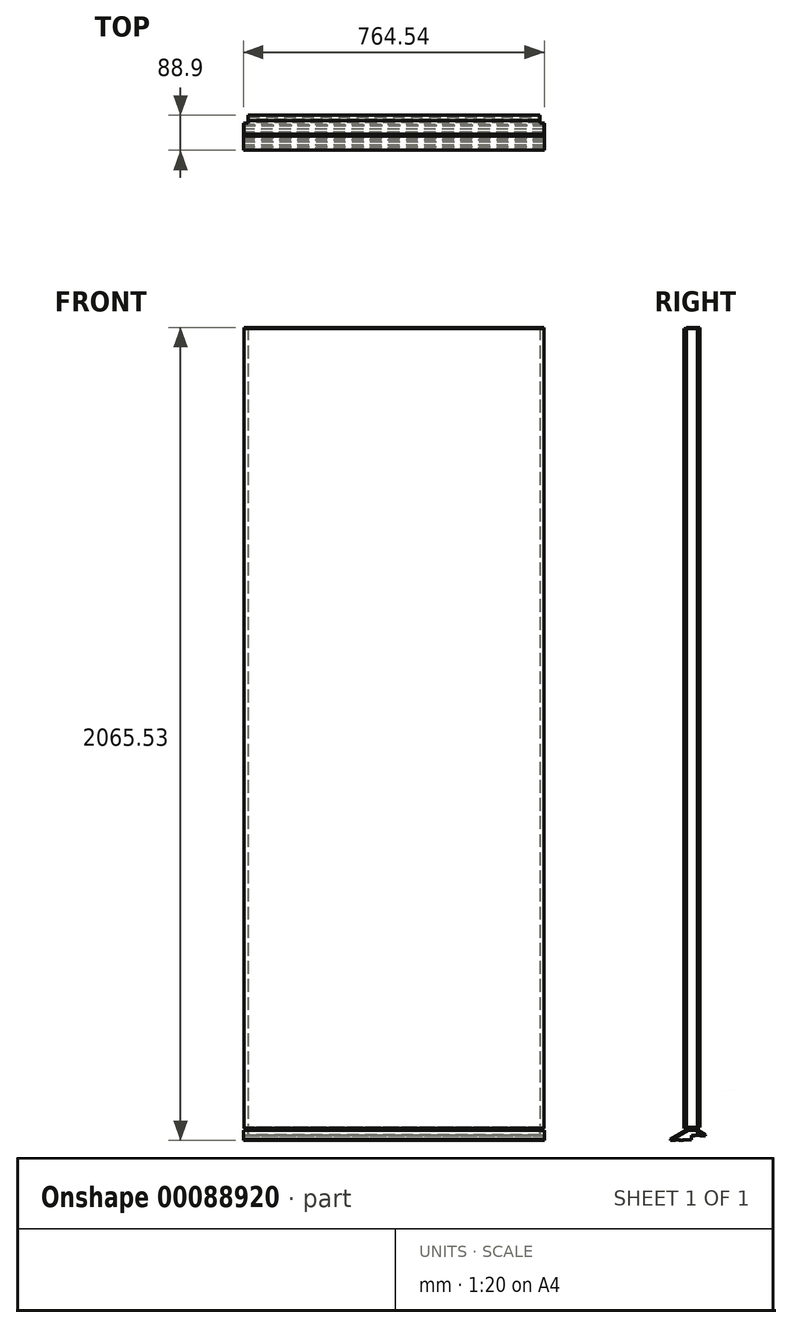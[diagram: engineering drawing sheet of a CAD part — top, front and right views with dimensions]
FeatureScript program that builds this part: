
annotation { "Feature Type Name" : "Feature", "Feature Type Description" : "" }
export const myFeature = defineFeature(function(context is Context, id is Id, definition is map)
    precondition{}
    {
        {
            var Q0;
            Q0=qCreatedBy(makeId("Right.planeOp"),FACE);
            var sketch = newSketch(context, id + "F0", { "sketchPlane" : qUnion([Q0])});
            skLineSegment(sketch, "E0.bottom", {"start": v(-1219.2, -50.8) * mm, "end": v(1219.2, -50.8) * mm});
            skLineSegment(sketch, "E0.top", {"start": v(-1219.2, 0) * mm, "end": v(1219.2, 0) * mm});
            skLineSegment(sketch, "E0.left", {"start": v(-1219.2, -50.8) * mm, "end": v(-1219.2, 0) * mm});
            skLineSegment(sketch, "E0.right", {"start": v(1219.2, -50.8) * mm, "end": v(1219.2, 0) * mm});
            skPoint(sketch, "E1", {"position": v(0, 0) * mm});
            skLineSegment(sketch, "E2", {"start": v(0, 0) * mm, "end": v(0, 11.43) * mm});
            skLineSegment(sketch, "E3", {"start": v(0, 11.43) * mm, "end": v(1219.2, 11.43) * mm});
            skLineSegment(sketch, "E4", {"start": v(1219.2, 11.43) * mm, "end": v(1219.2, 0) * mm});
            skLineSegment(sketch, "E5", {"start": v(0, 9.65) * mm, "end": v(1219.2, 9.65) * mm});
            skLineSegment(sketch, "E6.bottom", {"start": v(-18.03, 30.73) * mm, "end": v(16.5, 30.73) * mm});
            skLineSegment(sketch, "E6.top", {"start": v(-18.03, 2062.73) * mm, "end": v(16.5, 2062.73) * mm});
            skLineSegment(sketch, "E6.left", {"start": v(-18.03, 30.73) * mm, "end": v(-18.03, 2062.73) * mm});
            skLineSegment(sketch, "E6.right", {"start": v(16.5, 30.73) * mm, "end": v(16.5, 2062.73) * mm});
            skLineSegment(sketch, "E7", {"start": v(-18.03, 35.05) * mm, "end": v(16.5, 35.05) * mm});
            skLineSegment(sketch, "E8", {"start": v(6.35, 0) * mm, "end": v(6.35, 11.43) * mm});
            skSolve(sketch);
        }
        {
            var Q0;
            Q0=qCreatedBy(makeId("Right.planeOp"),FACE);
            var sketch = newSketch(context, id + "F1", { "sketchPlane" : qUnion([Q0])});
            skLineSegment(sketch, "E9.bottom", {"start": v(-1219.2, -50.8) * mm, "end": v(1219.2, -50.8) * mm});
            skLineSegment(sketch, "E9.top", {"start": v(-1219.2, 0) * mm, "end": v(1219.2, 0) * mm});
            skLineSegment(sketch, "E9.left", {"start": v(-1219.2, -50.8) * mm, "end": v(-1219.2, 0) * mm});
            skLineSegment(sketch, "E9.right", {"start": v(1219.2, -50.8) * mm, "end": v(1219.2, 0) * mm});
            skPoint(sketch, "E10", {"position": v(0, 0) * mm});
            skLineSegment(sketch, "E11", {"start": v(0, 0) * mm, "end": v(0, 11.94) * mm});
            skLineSegment(sketch, "E12", {"start": v(0, 11.94) * mm, "end": v(1219.2, 11.94) * mm});
            skLineSegment(sketch, "E13", {"start": v(1219.2, 11.94) * mm, "end": v(1219.2, 0) * mm});
            skLineSegment(sketch, "E14", {"start": v(0, 9.4) * mm, "end": v(1219.2, 9.4) * mm});
            skLineSegment(sketch, "E15.bottom", {"start": v(-12.45, 33.53) * mm, "end": v(22.1, 33.53) * mm});
            skLineSegment(sketch, "E15.top", {"start": v(-12.45, 2065.53) * mm, "end": v(22.1, 2065.53) * mm});
            skLineSegment(sketch, "E15.left", {"start": v(-12.45, 33.53) * mm, "end": v(-12.45, 2065.53) * mm});
            skLineSegment(sketch, "E15.right", {"start": v(22.1, 33.53) * mm, "end": v(22.1, 2065.53) * mm});
            skLineSegment(sketch, "E16", {"start": v(-12.45, 37.85) * mm, "end": v(22.1, 37.85) * mm});
            skLineSegment(sketch, "E17", {"start": v(9.4, 0) * mm, "end": v(9.4, 11.94) * mm});
            skSolve(sketch);
        }
        {
            var Q0;
            {var subQ0=sQuery(id+"F0.wireOp",EDGE,"E6.bottom");Q0=makeQuery(id+"F0.imprint","IMPRINT",FACE,{"disambiguationData":[TD([[makeQuery(id+"F0.imprint","IMPRINT",EDGE,{"derivedFrom":subQ0}),1.0]])]});}
            var Q1;
            {var subQ0=sQuery(id+"F0.wireOp",EDGE,"E6.top");Q1=makeQuery(id+"F0.imprint","IMPRINT",FACE,{"disambiguationData":[TD([[makeQuery(id+"F0.imprint","IMPRINT",EDGE,{"derivedFrom":subQ0}),-1.0]])]});}
            extrude(context, id + "F2", {"entities" : qUnion([Q0, Q1]), "endBound" : BoundingType.SYMMETRIC, "depth" : 762 * mm});
        }
        {
            var Q0;
            {var subQ0=sQuery(id+"F1.wireOp",EDGE,"E15.top");Q0=makeQuery(id+"F1.imprint","IMPRINT",FACE,{"disambiguationData":[TD([[makeQuery(id+"F1.imprint","IMPRINT",EDGE,{"derivedFrom":subQ0}),-1.0]])]});}
            var Q1;
            {var subQ0=sQuery(id+"F1.wireOp",EDGE,"E15.bottom");Q1=makeQuery(id+"F1.imprint","IMPRINT",FACE,{"disambiguationData":[TD([[makeQuery(id+"F1.imprint","IMPRINT",EDGE,{"derivedFrom":subQ0}),1.0]])]});}
            extrude(context, id + "F3", {"entities" : qUnion([Q0, Q1]), "endBound" : BoundingType.SYMMETRIC, "depth" : 762 * mm});
        }
        {
            var Q0;
            Q0=qCreatedBy(makeId("Right.planeOp"),FACE);
            var sketch = newSketch(context, id + "F4", { "sketchPlane" : qUnion([Q0])});
            skLineSegment(sketch, "E18", {"start": v(0, 11.83) * mm, "end": v(0, 0) * mm});
            skLineSegment(sketch, "E19", {"start": v(0, 0) * mm, "end": v(-9.31, 0) * mm});
            skLineSegment(sketch, "E20", {"start": v(-53.34, 0) * mm, "end": v(-53.34, 2.54) * mm});
            skLineSegment(sketch, "E21", {"start": v(-53.34, 2.54) * mm, "end": v(-13.75, 25.4) * mm});
            skLineSegment(sketch, "E22", {"start": v(-13.75, 25.4) * mm, "end": v(10.68, 25.4) * mm});
            skLineSegment(sketch, "E23", {"start": v(30.48, 11.43) * mm, "end": v(21.59, 11.43) * mm});
            skLineSegment(sketch, "E24", {"start": v(30.48, 11.43) * mm, "end": v(30.48, 13.97) * mm});
            skLineSegment(sketch, "E25", {"start": v(30.48, 13.97) * mm, "end": v(10.68, 25.4) * mm});
            skLineSegment(sketch, "E26", {"start": v(-44.03, 0) * mm, "end": v(-44.03, 0.8) * mm});
            skLineSegment(sketch, "E27", {"start": v(-44.03, 0.8) * mm, "end": v(-31.33, 0.8) * mm});
            skLineSegment(sketch, "E28", {"start": v(-22.01, 1.59) * mm, "end": v(-9.31, 1.59) * mm});
            skLineSegment(sketch, "E29", {"start": v(-9.31, 1.59) * mm, "end": v(-9.31, 0) * mm, "construction": true});
            skLineSegment(sketch, "E30.trimOffspring", {"start": v(-44.03, 0) * mm, "end": v(-53.34, 0) * mm});
            skLineSegment(sketch, "E31", {"start": v(8.89, 11.43) * mm, "end": v(8.89, 12.22) * mm, "construction": true});
            skLineSegment(sketch, "E32", {"start": v(8.89, 12.22) * mm, "end": v(21.59, 12.22) * mm});
            skLineSegment(sketch, "E33", {"start": v(21.59, 12.22) * mm, "end": v(21.59, 11.43) * mm});
            skLineSegment(sketch, "E34", {"start": v(8.89, 11.43) * mm, "end": v(8.89, 10.64) * mm, "construction": true});
            skLineSegment(sketch, "E35", {"start": v(8.89, 10.64) * mm, "end": v(21.59, 10.64) * mm, "construction": true});
            skLineSegment(sketch, "E36", {"start": v(21.59, 10.64) * mm, "end": v(21.59, 11.43) * mm, "construction": true});
            skLineSegment(sketch, "E37", {"start": v(-44.03, 0) * mm, "end": v(-44.03, -0.8) * mm, "construction": true});
            skLineSegment(sketch, "E38", {"start": v(-44.03, -0.8) * mm, "end": v(-31.33, -0.8) * mm, "construction": true});
            skLineSegment(sketch, "E39", {"start": v(-31.33, -0.8) * mm, "end": v(-31.33, 0) * mm, "construction": true});
            skLineSegment(sketch, "E40", {"start": v(-22.01, 0) * mm, "end": v(-22.01, -1.59) * mm, "construction": true});
            skLineSegment(sketch, "E41", {"start": v(-22.01, -1.59) * mm, "end": v(-9.31, -1.59) * mm, "construction": true});
            skLineSegment(sketch, "E42", {"start": v(-9.31, -1.59) * mm, "end": v(-9.31, 0) * mm, "construction": true});
            skLineSegment(sketch, "E43", {"start": v(-31.33, 0.8) * mm, "end": v(-31.33, 0) * mm, "construction": true});
            skLineSegment(sketch, "E44", {"start": v(-22.01, 1.59) * mm, "end": v(-22.01, 0) * mm, "construction": true});
            skLineSegment(sketch, "E45", {"start": v(-31.33, 0.8) * mm, "end": v(-31.33, 0.4) * mm});
            skLineSegment(sketch, "E46", {"start": v(-31.33, 0.4) * mm, "end": v(-22.01, 0.4) * mm});
            skLineSegment(sketch, "E47", {"start": v(-22.01, 0.4) * mm, "end": v(-22.01, 1.59) * mm});
            skLineSegment(sketch, "E48", {"start": v(-9.31, 0.8) * mm, "end": v(0, 0.8) * mm});
            skLineSegment(sketch, "E49", {"start": v(-9.31, 1.59) * mm, "end": v(-9.31, 0.8) * mm});
            skLineSegment(sketch, "E50", {"start": v(8.89, 11.83) * mm, "end": v(0, 11.83) * mm});
            skLineSegment(sketch, "E51", {"start": v(8.89, 12.22) * mm, "end": v(8.89, 11.83) * mm});
            skSolve(sketch);
        }
        {
            var Q0;
            Q0=qCreatedBy(makeId("Right.planeOp"),FACE);
            var sketch = newSketch(context, id + "F5", { "sketchPlane" : qUnion([Q0])});
            skLineSegment(sketch, "E52", {"start": v(-48.26, 0) * mm, "end": v(-48.26, 2.54) * mm});
            skLineSegment(sketch, "E53", {"start": v(-48.26, 2.54) * mm, "end": v(-8.67, 25.4) * mm});
            skLineSegment(sketch, "E54", {"start": v(-8.67, 25.4) * mm, "end": v(16.64, 25.4) * mm});
            skLineSegment(sketch, "E55", {"start": v(24.13, 11.94) * mm, "end": v(35.56, 11.94) * mm});
            skLineSegment(sketch, "E56", {"start": v(35.56, 11.94) * mm, "end": v(35.56, 14.48) * mm});
            skLineSegment(sketch, "E57", {"start": v(16.64, 25.4) * mm, "end": v(35.56, 14.48) * mm});
            skLineSegment(sketch, "E58", {"start": v(-40.64, 0) * mm, "end": v(-40.64, 0.8) * mm});
            skLineSegment(sketch, "E59", {"start": v(-40.64, 0.8) * mm, "end": v(-27.94, 0.8) * mm});
            skLineSegment(sketch, "E60", {"start": v(-20.32, 0) * mm, "end": v(-20.32, 1.59) * mm});
            skLineSegment(sketch, "E61", {"start": v(-20.32, 1.59) * mm, "end": v(-7.62, 1.59) * mm});
            skLineSegment(sketch, "E62.trimOffspring", {"start": v(-40.64, 0) * mm, "end": v(-48.26, 0) * mm});
            skLineSegment(sketch, "E63", {"start": v(11.43, 12.2) * mm, "end": v(11.43, 12.47) * mm});
            skLineSegment(sketch, "E64", {"start": v(11.43, 12.47) * mm, "end": v(24.13, 12.47) * mm});
            skLineSegment(sketch, "E65", {"start": v(24.13, 12.47) * mm, "end": v(24.13, 11.94) * mm});
            skLineSegment(sketch, "E66.trimOffspring", {"start": v(0, 12.2) * mm, "end": v(11.43, 12.2) * mm});
            skLineSegment(sketch, "E67", {"start": v(-40.64, 0.8) * mm, "end": v(-48.26, 0.8) * mm, "construction": true});
            skLineSegment(sketch, "E68", {"start": v(-7.62, 1.59) * mm, "end": v(0, 1.59) * mm, "construction": true});
            skLineSegment(sketch, "E69", {"start": v(11.43, 12.2) * mm, "end": v(11.43, 11.4) * mm, "construction": true});
            skLineSegment(sketch, "E70", {"start": v(11.43, 11.4) * mm, "end": v(24.13, 11.4) * mm, "construction": true});
            skLineSegment(sketch, "E71", {"start": v(24.13, 11.4) * mm, "end": v(24.13, 11.94) * mm, "construction": true});
            skLineSegment(sketch, "E72", {"start": v(-40.64, 0) * mm, "end": v(-40.64, -0.8) * mm, "construction": true});
            skLineSegment(sketch, "E73", {"start": v(-40.64, -0.8) * mm, "end": v(-27.94, -0.8) * mm, "construction": true});
            skLineSegment(sketch, "E74", {"start": v(-27.94, -0.8) * mm, "end": v(-27.94, 0) * mm, "construction": true});
            skLineSegment(sketch, "E75", {"start": v(-20.32, 0) * mm, "end": v(-20.32, -1.59) * mm, "construction": true});
            skLineSegment(sketch, "E76", {"start": v(-20.32, -1.59) * mm, "end": v(-7.62, -1.59) * mm, "construction": true});
            skLineSegment(sketch, "E77", {"start": v(-7.62, -1.59) * mm, "end": v(-7.62, 0) * mm, "construction": true});
            skLineSegment(sketch, "E78", {"start": v(0, 12.47) * mm, "end": v(11.43, 12.47) * mm, "construction": true});
            skLineSegment(sketch, "E79", {"start": v(24.13, 12.47) * mm, "end": v(35.56, 12.47) * mm, "construction": true});
            skLineSegment(sketch, "E80", {"start": v(-27.94, 0.8) * mm, "end": v(-20.32, 0.8) * mm, "construction": true});
            skLineSegment(sketch, "E81", {"start": v(0, 0.8) * mm, "end": v(0, 12.2) * mm});
            skLineSegment(sketch, "E82", {"start": v(-7.62, 1.59) * mm, "end": v(-7.62, 0.8) * mm});
            skLineSegment(sketch, "E83", {"start": v(-7.62, 0.8) * mm, "end": v(0, 0.8) * mm});
            skLineSegment(sketch, "E84", {"start": v(-27.94, 0.8) * mm, "end": v(-27.94, 0.4) * mm});
            skLineSegment(sketch, "E85", {"start": v(-27.94, 0.4) * mm, "end": v(-20.32, 0.4) * mm});
            skPoint(sketch, "E86", {"position": v(-40.64, 0.4) * mm});
            skPoint(sketch, "E87", {"position": v(24.13, 12.2) * mm});
            skSolve(sketch);
        }
        {
            var Q0;
            Q0=makeQuery(id+"F4.imprint","IMPRINT",FACE,{"disambiguationData":[TD([[makeQuery(id+"F4.imprint","IMPRINT",EDGE,{"derivedFrom":sQuery(id+"F4.wireOp",EDGE,"E18")}),-1.0]])]});
            extrude(context, id + "F6", {"entities" : qUnion([Q0]), "endBound" : BoundingType.SYMMETRIC, "oppositeDirection" : true, "depth" : 764.54 * mm});
        }
        {
            var Q0;
            Q0=makeQuery(id+"F5.imprint","IMPRINT",FACE,{"disambiguationData":[TD([[makeQuery(id+"F5.imprint","IMPRINT",EDGE,{"derivedFrom":sQuery(id+"F5.wireOp",EDGE,"E52")}),-1.0]])]});
            extrude(context, id + "F7", {"entities" : qUnion([Q0]), "endBound" : BoundingType.SYMMETRIC, "depth" : 764.54 * mm});
        }
        {
            var Q0;
            Q0=qCreatedBy(makeId("Top.planeOp"),FACE);
            var sketch = newSketch(context, id + "F8", { "sketchPlane" : qUnion([Q0])});
            skLineSegment(sketch, "E88.0", {"start": v(381, 16.5) * mm, "end": v(-381, 16.5) * mm, "construction": true});
            skLineSegment(sketch, "E88.1", {"start": v(-381, -18.03) * mm, "end": v(-381, 16.5) * mm, "construction": true});
            skLineSegment(sketch, "E88.2", {"start": v(381, -18.03) * mm, "end": v(-381, -18.03) * mm, "construction": true});
            skLineSegment(sketch, "E88.3", {"start": v(381, -18.03) * mm, "end": v(381, 16.5) * mm, "construction": true});
            skLineSegment(sketch, "E89", {"start": v(0, 16.5) * mm, "end": v(0, -18.03) * mm, "construction": true});
            skLineSegment(sketch, "E90.bottom", {"start": v(-381, 16.5) * mm, "end": v(-372.11, 16.5) * mm, "construction": true});
            skLineSegment(sketch, "E90.top", {"start": v(-381, 67.3) * mm, "end": v(-372.11, 67.3) * mm, "construction": true});
            skLineSegment(sketch, "E90.left", {"start": v(-381, 16.5) * mm, "end": v(-381, 67.3) * mm, "construction": true});
            skLineSegment(sketch, "E90.right", {"start": v(-372.11, 16.5) * mm, "end": v(-372.11, 67.3) * mm, "construction": true});
            skLineSegment(sketch, "E91.0", {"start": v(-382.27, 15.24) * mm, "end": v(-382.27, 68.58) * mm});
            skLineSegment(sketch, "E91.1", {"start": v(-382.27, 15.24) * mm, "end": v(-370.84, 15.24) * mm});
            skLineSegment(sketch, "E91.2", {"start": v(-370.84, 15.24) * mm, "end": v(-370.84, 68.58) * mm});
            skLineSegment(sketch, "E91.3", {"start": v(-382.27, 68.58) * mm, "end": v(-370.84, 68.58) * mm});
            skLineSegment(sketch, "E92.MirrorCS", {"start": v(382.27, 15.24) * mm, "end": v(382.27, 68.58) * mm});
            skLineSegment(sketch, "E93.MirrorCS", {"start": v(382.27, 15.24) * mm, "end": v(370.84, 15.24) * mm});
            skLineSegment(sketch, "E94.MirrorCS", {"start": v(370.84, 15.24) * mm, "end": v(370.84, 68.58) * mm});
            skLineSegment(sketch, "E95.MirrorCS", {"start": v(382.27, 68.58) * mm, "end": v(370.84, 68.58) * mm});
            skSolve(sketch);
        }
        {
            var Q0;
            Q0=qCreatedBy(makeId("Top.planeOp"),FACE);
            var sketch = newSketch(context, id + "F9", { "sketchPlane" : qUnion([Q0])});
            skLineSegment(sketch, "E96.0", {"start": v(381, -12.45) * mm, "end": v(381, 22.1) * mm, "construction": true});
            skLineSegment(sketch, "E96.1", {"start": v(381, 22.1) * mm, "end": v(-381, 22.1) * mm, "construction": true});
            skLineSegment(sketch, "E96.2", {"start": v(381, -12.45) * mm, "end": v(-381, -12.45) * mm, "construction": true});
            skLineSegment(sketch, "E96.3", {"start": v(-381, -12.45) * mm, "end": v(-381, 22.1) * mm, "construction": true});
            skLineSegment(sketch, "E97", {"start": v(0, 22.1) * mm, "end": v(0, -12.45) * mm, "construction": true});
            skLineSegment(sketch, "E98.bottom", {"start": v(-381, 22.1) * mm, "end": v(-372.11, 22.1) * mm, "construction": true});
            skLineSegment(sketch, "E98.top", {"start": v(-381, 72.9) * mm, "end": v(-372.11, 72.9) * mm, "construction": true});
            skLineSegment(sketch, "E98.left", {"start": v(-381, 22.1) * mm, "end": v(-381, 72.9) * mm, "construction": true});
            skLineSegment(sketch, "E98.right", {"start": v(-372.11, 22.1) * mm, "end": v(-372.11, 72.9) * mm, "construction": true});
            skLineSegment(sketch, "E99.0", {"start": v(-370.84, 20.83) * mm, "end": v(-370.84, 74.17) * mm});
            skLineSegment(sketch, "E99.1", {"start": v(-382.27, 20.83) * mm, "end": v(-370.84, 20.83) * mm});
            skLineSegment(sketch, "E99.2", {"start": v(-382.27, 20.83) * mm, "end": v(-382.27, 74.17) * mm});
            skLineSegment(sketch, "E99.3", {"start": v(-382.27, 74.17) * mm, "end": v(-370.84, 74.17) * mm});
            skLineSegment(sketch, "E100.MirrorCS", {"start": v(382.27, 74.17) * mm, "end": v(370.84, 74.17) * mm});
            skLineSegment(sketch, "E101.MirrorCS", {"start": v(370.84, 20.83) * mm, "end": v(370.84, 74.17) * mm});
            skLineSegment(sketch, "E102.MirrorCS", {"start": v(382.27, 20.83) * mm, "end": v(382.27, 74.17) * mm});
            skLineSegment(sketch, "E103.MirrorCS", {"start": v(382.27, 20.83) * mm, "end": v(370.84, 20.83) * mm});
            skSolve(sketch);
        }
        {
            var Q0;
            Q0=makeQuery(id+"F8.imprint","IMPRINT",FACE,{"disambiguationData":[TD([[makeQuery(id+"F8.imprint","IMPRINT",EDGE,{"derivedFrom":sQuery(id+"F8.wireOp",EDGE,"E91.0")}),-1.0]])]});
            var Q1;
            Q1=makeQuery(id+"F8.imprint","IMPRINT",FACE,{"disambiguationData":[TD([[makeQuery(id+"F8.imprint","IMPRINT",EDGE,{"derivedFrom":sQuery(id+"F8.wireOp",EDGE,"E92.MirrorCS")}),1.0]])]});
            extrude(context, id + "F10", {"entities" : qUnion([Q0, Q1]), "operationType" : NewBodyOperationType.REMOVE, "endBound" : BoundingType.THROUGH_ALL, "depth" : 25.4 * mm});
        }
        {
            var Q0;
            Q0=makeQuery(id+"F9.imprint","IMPRINT",FACE,{"disambiguationData":[TD([[makeQuery(id+"F9.imprint","IMPRINT",EDGE,{"derivedFrom":sQuery(id+"F9.wireOp",EDGE,"E99.0")}),1.0]])]});
            var Q1;
            Q1=makeQuery(id+"F9.imprint","IMPRINT",FACE,{"disambiguationData":[TD([[makeQuery(id+"F9.imprint","IMPRINT",EDGE,{"derivedFrom":sQuery(id+"F9.wireOp",EDGE,"E100.MirrorCS")}),1.0]])]});
            extrude(context, id + "F11", {"entities" : qUnion([Q0, Q1]), "operationType" : NewBodyOperationType.REMOVE, "endBound" : BoundingType.THROUGH_ALL, "depth" : 25.4 * mm});
        }
    });
